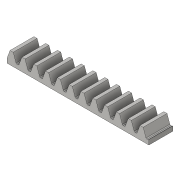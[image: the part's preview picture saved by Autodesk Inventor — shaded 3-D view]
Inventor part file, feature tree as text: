
AUTODESK INVENTOR PART (.ipt)
format: ipt  version: 2016 (Build 200138000, 138)  size: 228,864 bytes
history: native  units: in
note: dims shown in document units (in); Inventor stores cm internally (conversion verified against a paired STEP export)
features: sketch x3, extrude x2
ambient origin geometry x8: Origin, YZ Plane, XZ Plane, XY Plane, X Axis, Y Axis, Z Axis, Center Point
bodies: Solid1 (feature_tree)
feature tree (5):
  extrude  "Extrusion1"  Depth=0.5in
  sketch  "Sketch2"  dims[d4=3.0562in d5=2.9447in]
  extrude  "Extrusion2"  Depth=2.9447in
  sketch  "Sketch1"  dims[d0=0.5in d1=0.0in d3=0.5391in]
  sketch  "Sketch3"  dims[d6=1.0in d7=0.0in]
